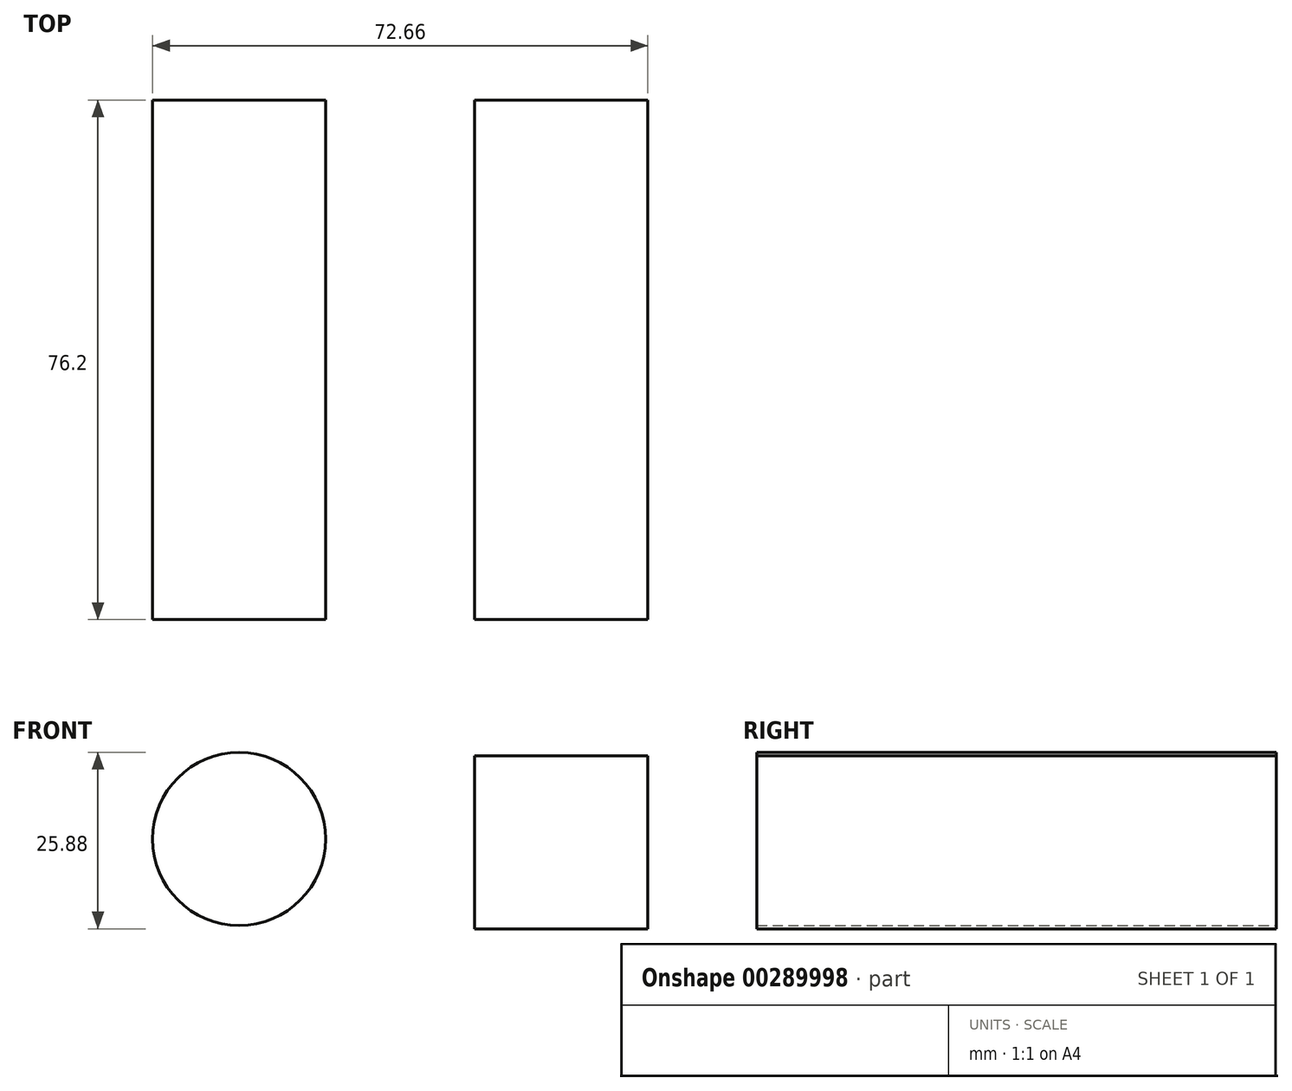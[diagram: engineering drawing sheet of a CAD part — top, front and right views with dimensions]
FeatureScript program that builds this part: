
annotation { "Feature Type Name" : "Feature", "Feature Type Description" : "" }
export const myFeature = defineFeature(function(context is Context, id is Id, definition is map)
    precondition{}
    {
        {
            var Q0;
            Q0=qCreatedBy(makeId("Front.planeOp"),FACE);
            var sketch = newSketch(context, id + "F0", { "sketchPlane" : qUnion([Q0])});
            skCircle(sketch, "E0", {"center": v(-68.93, 39.9) * mm, "radius": 12.7 * mm});
            skLineSegment(sketch, "E1.bottom", {"start": v(-8.97, 26.73) * mm, "end": v(-34.37, 26.73) * mm});
            skLineSegment(sketch, "E1.top", {"start": v(-8.97, 52.13) * mm, "end": v(-34.37, 52.13) * mm});
            skLineSegment(sketch, "E1.left", {"start": v(-8.97, 26.73) * mm, "end": v(-8.97, 52.13) * mm});
            skLineSegment(sketch, "E1.right", {"start": v(-34.37, 26.73) * mm, "end": v(-34.37, 52.13) * mm});
            skSolve(sketch);
        }
        {
            var Q0;
            Q0 = qSketchRegion(id + "F0", true);
            extrude(context, id + "F1", {"entities" : qUnion([Q0]), "depth" : 76.2 * mm});
        }
    });
